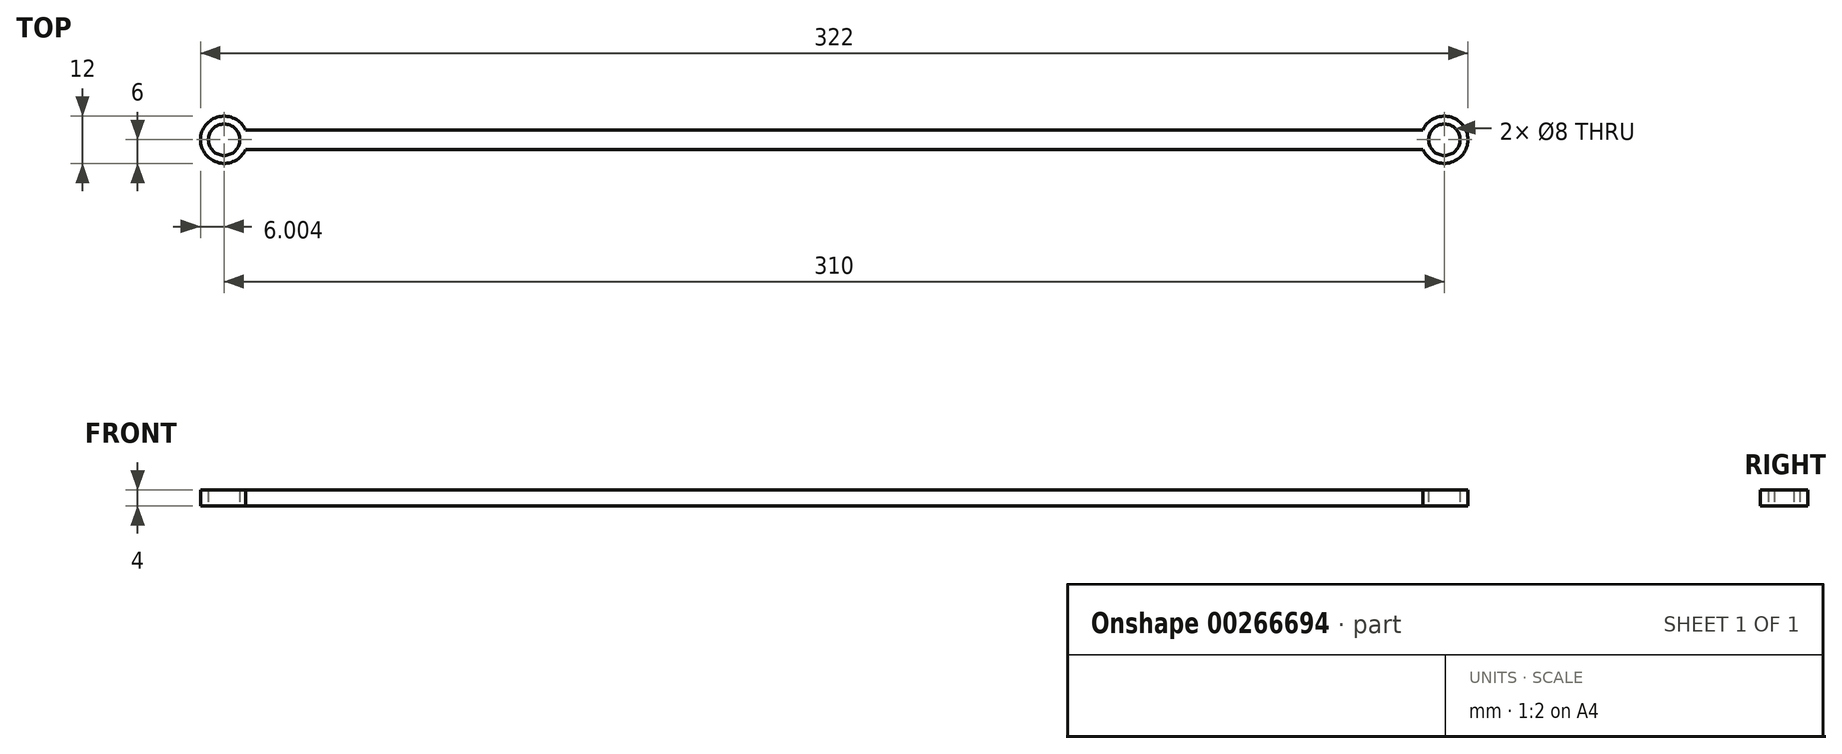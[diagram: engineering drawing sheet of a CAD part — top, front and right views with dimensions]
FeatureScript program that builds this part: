
annotation { "Feature Type Name" : "Feature", "Feature Type Description" : "" }
export const myFeature = defineFeature(function(context is Context, id is Id, definition is map)
    precondition{}
    {
        {
            var Q0;
            Q0=qCreatedBy(makeId("Top.planeOp"),FACE);
            var sketch = newSketch(context, id + "F0", { "sketchPlane" : qUnion([Q0])});
            skLineSegment(sketch, "E0", {"start": v(-148.18, 2.5) * mm, "end": v(150.9, 2.5) * mm});
            skLineSegment(sketch, "E1", {"start": v(-148.18, -2.5) * mm, "end": v(150.9, -2.5) * mm});
            skLineSegment(sketch, "E2", {"start": v(1.36, 2.5) * mm, "end": v(1.36, -2.5) * mm, "construction": true});
            skArc(sketch, "E3", {"start": v(-148.18, 2.5) * mm, "mid": v(-159.64, 0) * mm, "end": v(-148.18, -2.5) * mm});
            skArc(sketch, "E4", {"start": v(150.9, -2.5) * mm, "mid": v(162.36, 0) * mm, "end": v(150.9, 2.5) * mm});
            skCircle(sketch, "E5", {"center": v(-153.64, 0) * mm, "radius": 4 * mm});
            skCircle(sketch, "E6", {"center": v(156.36, 0) * mm, "radius": 4 * mm});
            skSolve(sketch);
        }
        {
            var Q0;
            Q0=qSketchRegion(id+"F0",true);
            extrude(context, id + "F1", {"entities" : qUnion([Q0]), "depth" : 4 * mm});
        }
    });
